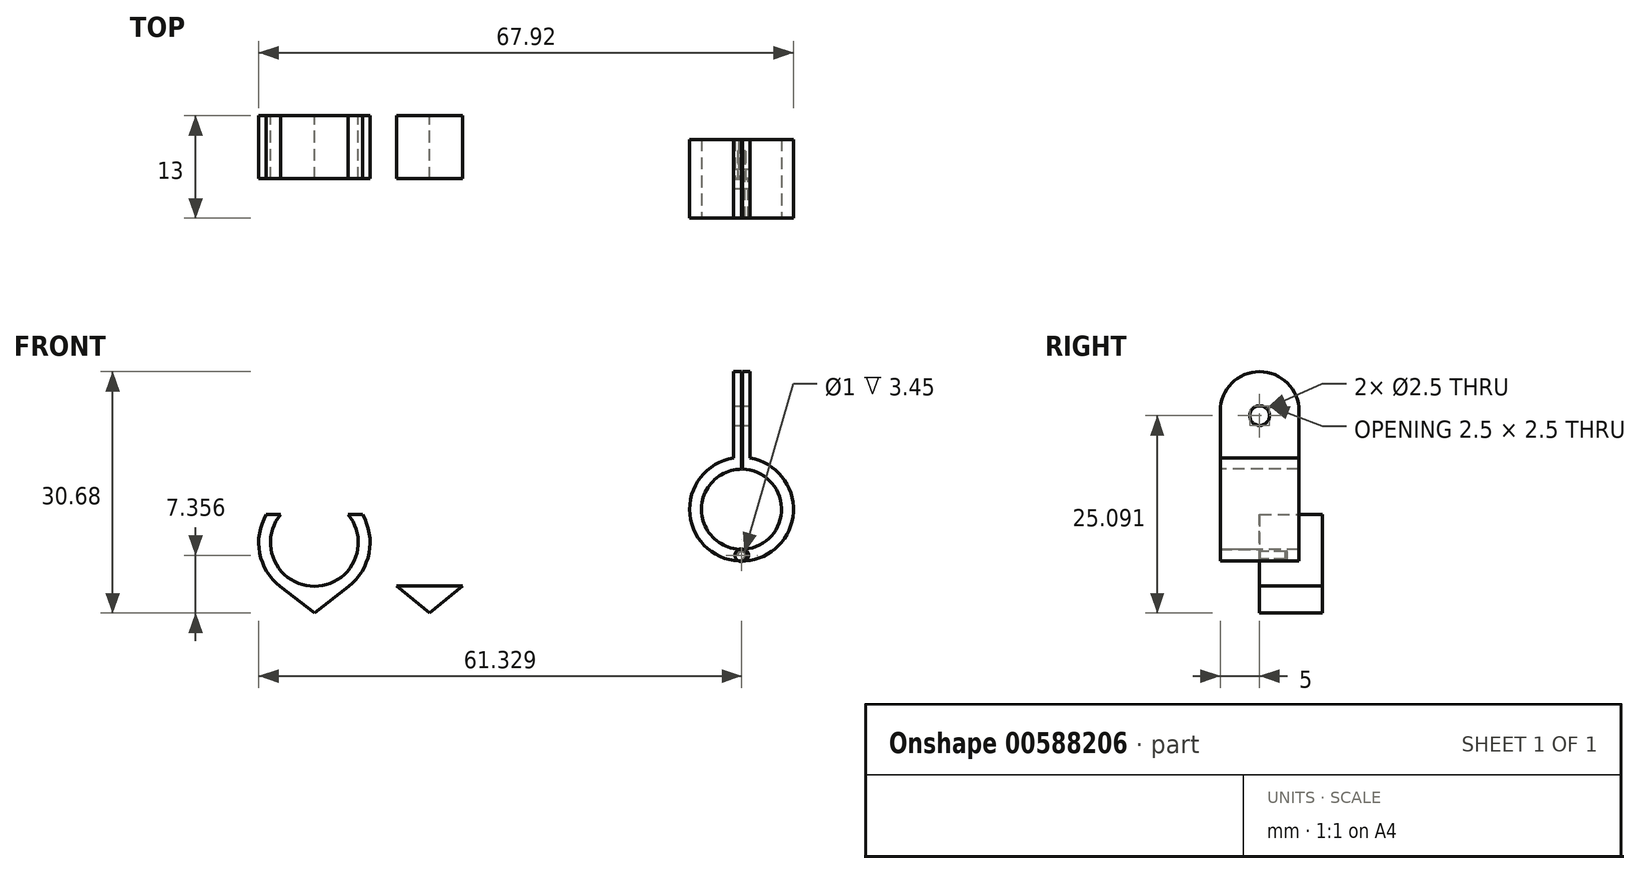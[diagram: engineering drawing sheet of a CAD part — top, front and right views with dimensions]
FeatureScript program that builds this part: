
annotation { "Feature Type Name" : "Feature", "Feature Type Description" : "" }
export const myFeature = defineFeature(function(context is Context, id is Id, definition is map)
    precondition{}
    {
        {
            var Q0;
            Q0=qCreatedBy(makeId("Front.planeOp"),FACE);
            var sketch = newSketch(context, id + "F0", { "sketchPlane" : qUnion([Q0])});
            skArc(sketch, "E0", {"start": v(-6.1, 12.53) * mm, "mid": v(0, 1.9) * mm, "end": v(6.1, 12.53) * mm});
            skLineSegment(sketch, "E1", {"start": v(-4.35, 3.4) * mm, "end": v(0, 0) * mm});
            skLineSegment(sketch, "E2", {"start": v(0, 0) * mm, "end": v(4.35, 3.4) * mm});
            skLineSegment(sketch, "E3", {"start": v(6.1, 12.53) * mm, "end": v(-6.1, 12.53) * mm});
            skArc(sketch, "E4.0", {"start": v(-4.29, 12.53) * mm, "mid": v(0, 3.4) * mm, "end": v(4.29, 12.53) * mm});
            skLineSegment(sketch, "E5", {"start": v(-5, 0) * mm, "end": v(5, 0) * mm});
            skArc(sketch, "E6", {"start": v(8.79, 11.53) * mm, "mid": v(14.66, 1.94) * mm, "end": v(20.53, 11.53) * mm});
            skLineSegment(sketch, "E7", {"start": v(10.47, 3.44) * mm, "end": v(14.66, 0) * mm});
            skLineSegment(sketch, "E8", {"start": v(14.66, 0) * mm, "end": v(18.84, 3.44) * mm});
            skLineSegment(sketch, "E9", {"start": v(20.53, 11.53) * mm, "end": v(8.79, 11.53) * mm});
            skArc(sketch, "E10.0", {"start": v(10.54, 11.53) * mm, "mid": v(14.66, 3.44) * mm, "end": v(18.78, 11.53) * mm});
            skLineSegment(sketch, "E11", {"start": v(9.66, 0) * mm, "end": v(19.66, 0) * mm});
            skLineSegment(sketch, "E12", {"start": v(14.66, 8.53) * mm, "end": v(14.66, 0) * mm});
            skLineSegment(sketch, "E13", {"start": v(-4.35, 3.4) * mm, "end": v(4.35, 3.4) * mm});
            skLineSegment(sketch, "E14", {"start": v(0, 8.97) * mm, "end": v(0, 0) * mm});
            skLineSegment(sketch, "E15", {"start": v(10.47, 3.44) * mm, "end": v(18.84, 3.44) * mm});
            skArc(sketch, "E16", {"start": v(34.1, 19.13) * mm, "mid": v(34.04, 8) * mm, "end": v(34.2, 19.13) * mm});
            skArc(sketch, "E17", {"start": v(33.1, 20.56) * mm, "mid": v(34.04, 6.5) * mm, "end": v(35.2, 20.55) * mm});
            skLineSegment(sketch, "E18", {"start": v(33.1, 19.04) * mm, "end": v(33.1, 31.04) * mm});
            skLineSegment(sketch, "E19", {"start": v(33.1, 31.04) * mm, "end": v(34.1, 31.04) * mm});
            skLineSegment(sketch, "E20", {"start": v(34.1, 31.04) * mm, "end": v(34.1, 19.13) * mm});
            skLineSegment(sketch, "E21", {"start": v(35.2, 19.02) * mm, "end": v(35.2, 31.04) * mm});
            skLineSegment(sketch, "E22", {"start": v(35.2, 31.04) * mm, "end": v(34.2, 31.04) * mm});
            skLineSegment(sketch, "E23", {"start": v(34.2, 31.04) * mm, "end": v(34.2, 19.13) * mm});
            skArc(sketch, "E24", {"start": v(53.26, 19.7) * mm, "mid": v(54.2, 6.6) * mm, "end": v(55.36, 19.7) * mm});
            skLineSegment(sketch, "E25", {"start": v(53.26, 18.19) * mm, "end": v(53.26, 30.68) * mm});
            skLineSegment(sketch, "E26", {"start": v(53.26, 30.68) * mm, "end": v(54.26, 30.68) * mm});
            skLineSegment(sketch, "E27", {"start": v(54.26, 30.68) * mm, "end": v(54.26, 18.29) * mm});
            skLineSegment(sketch, "E28", {"start": v(55.36, 18.17) * mm, "end": v(55.36, 30.68) * mm});
            skLineSegment(sketch, "E29", {"start": v(55.36, 30.68) * mm, "end": v(54.36, 30.68) * mm});
            skLineSegment(sketch, "E30", {"start": v(54.36, 30.68) * mm, "end": v(54.36, 18.28) * mm});
            skArc(sketch, "E31", {"start": v(54.26, 18.29) * mm, "mid": v(54.2, 8.1) * mm, "end": v(54.36, 18.28) * mm});
            skCircle(sketch, "E32", {"center": v(34.1, 7.24) * mm, "radius": 0.5 * mm});
            skCircle(sketch, "E33", {"center": v(54.26, 7.36) * mm, "radius": 0.5 * mm});
            skCircle(sketch, "E34", {"center": v(34.1, 7.24) * mm, "radius": 0.45 * mm});
            skCircle(sketch, "E35", {"center": v(54.26, 7.36) * mm, "radius": 0.45 * mm});
            skLineSegment(sketch, "E36", {"start": v(34.1, 8) * mm, "end": v(34.1, 6.5) * mm});
            skLineSegment(sketch, "E37", {"start": v(54.26, 8.1) * mm, "end": v(54.26, 7.86) * mm});
            skLineSegment(sketch, "E38.trimOffspring", {"start": v(54.26, 6.86) * mm, "end": v(54.26, 6.6) * mm});
            skArc(sketch, "E39", {"start": v(54, 8.11) * mm, "mid": v(53.42, 7.38) * mm, "end": v(53.97, 6.61) * mm});
            skArc(sketch, "E40", {"start": v(54.58, 6.61) * mm, "mid": v(55.09, 7.36) * mm, "end": v(54.59, 8.12) * mm});
            skArc(sketch, "E41", {"start": v(53.92, 8.12) * mm, "mid": v(53.36, 7.39) * mm, "end": v(53.86, 6.62) * mm});
            skArc(sketch, "E42", {"start": v(54.7, 6.62) * mm, "mid": v(55.15, 7.38) * mm, "end": v(54.68, 8.12) * mm});
            skSolve(sketch);
        }
        {
            var Q0;
            Q0=sQuery(id+"F0.wireOp",EDGE,"E5");
            var Q1;
            {var subQ0=sQuery(id+"F0.wireOp",EDGE,"E1");Q1=makeQuery(id+"F0.imprint","IMPRINT",FACE,{"disambiguationData":[TD([[makeQuery(id+"F0.imprint","IMPRINT",EDGE,{"derivedFrom":subQ0}),1.0]])]});}
            cPlane(context, id + "F1", {"entities" : qUnion([Q0, Q1]), "cplaneType" : CPlaneType.LINE_ANGLE, "offset" : 25 * mm, "angle" : 90 * degree, "width" : 150 * mm, "height" : 150 * mm});
        }
        {
            var Q0;
            Q0=qCreatedBy(id+"F1.planeOp",FACE);
            var sketch = newSketch(context, id + "F2", { "sketchPlane" : qUnion([Q0])});
            skLineSegment(sketch, "E43", {"start": v(0, 0) * mm, "end": v(0, 8) * mm});
            skLineSegment(sketch, "E44.0", {"start": v(9.66, 0) * mm, "end": v(19.66, 0) * mm});
            skLineSegment(sketch, "E45", {"start": v(14.66, 0) * mm, "end": v(14.66, 8) * mm});
            skSolve(sketch);
        }
        {
            var Q0;
            {var subQ0=sQuery(id+"F0.wireOp",EDGE,"E3");var subQ1=sQuery(id+"F0.wireOp",EDGE,"E0");var subQ2=makeQuery(id+"F0.imprint","INTERSECT",VERTEX,{"disambiguationData":[OD(0.0)],"derivedFrom":[subQ1,subQ0]});Q0=makeQuery(id+"F0.imprint","IMPRINT",FACE,{"disambiguationData":[TD([[makeQuery(id+"F0.imprint","IMPRINT",EDGE,{"disambiguationData":[TD([[subQ2,1.0]])],"derivedFrom":subQ0}),1.0]])]});}
            var Q1;
            {var subQ1=sQuery(id+"F0.wireOp",EDGE,"E0");var subQ3=sQuery(id+"F0.wireOp",EDGE,"E14");var subQ4=makeQuery(id+"F0.imprint","INTERSECT",VERTEX,{"derivedFrom":[subQ1,subQ3]});Q1=makeQuery(id+"F0.imprint","IMPRINT",FACE,{"disambiguationData":[TD([[makeQuery(id+"F0.imprint","IMPRINT",EDGE,{"disambiguationData":[TD([[subQ4,1.0]])],"derivedFrom":subQ1}),1.0]])]});}
            var Q2;
            {var subQ0=sQuery(id+"F0.wireOp",EDGE,"E1");Q2=makeQuery(id+"F0.imprint","IMPRINT",FACE,{"disambiguationData":[TD([[makeQuery(id+"F0.imprint","IMPRINT",EDGE,{"derivedFrom":subQ0}),1.0]])]});}
            var Q3;
            {var subQ0=sQuery(id+"F0.wireOp",EDGE,"E2");Q3=makeQuery(id+"F0.imprint","IMPRINT",FACE,{"disambiguationData":[TD([[makeQuery(id+"F0.imprint","IMPRINT",EDGE,{"derivedFrom":subQ0}),1.0]])]});}
            var Q4;
            {var subQ1=sQuery(id+"F0.wireOp",EDGE,"E0");var subQ3=sQuery(id+"F0.wireOp",EDGE,"E14");var subQ4=makeQuery(id+"F0.imprint","INTERSECT",VERTEX,{"derivedFrom":[subQ1,subQ3]});Q4=makeQuery(id+"F0.imprint","IMPRINT",FACE,{"disambiguationData":[TD([[makeQuery(id+"F0.imprint","IMPRINT",EDGE,{"disambiguationData":[TD([[subQ4,-1.0]])],"derivedFrom":subQ1}),1.0]])]});}
            var Q5;
            {var subQ0=sQuery(id+"F0.wireOp",EDGE,"E3");var subQ1=sQuery(id+"F0.wireOp",EDGE,"E0");var subQ2=makeQuery(id+"F0.imprint","INTERSECT",VERTEX,{"disambiguationData":[OD(1.0)],"derivedFrom":[subQ1,subQ0]});Q5=makeQuery(id+"F0.imprint","IMPRINT",FACE,{"disambiguationData":[TD([[makeQuery(id+"F0.imprint","IMPRINT",EDGE,{"disambiguationData":[TD([[subQ2,-1.0]])],"derivedFrom":subQ0}),1.0]])]});}
            var Q6;
            Q6=sQuery(id+"F2.wireOp",EDGE,"E43");
            sweep(context, id + "F3", {"profiles" : qUnion([Q0, Q1, Q2, Q3, Q4, Q5]), "path" : qUnion([Q6])});
        }
        {
            var Q0;
            {var subQ0=sQuery(id+"F0.wireOp",EDGE,"E9");var subQ1=sQuery(id+"F0.wireOp",EDGE,"E6");var subQ2=makeQuery(id+"F0.imprint","INTERSECT",VERTEX,{"disambiguationData":[OD(0.0)],"derivedFrom":[subQ1,subQ0]});Q0=makeQuery(id+"F0.imprint","IMPRINT",FACE,{"disambiguationData":[TD([[makeQuery(id+"F0.imprint","IMPRINT",EDGE,{"disambiguationData":[TD([[subQ2,1.0]])],"derivedFrom":subQ0}),1.0]])]});}
            var Q1;
            {var subQ1=sQuery(id+"F0.wireOp",EDGE,"E6");var subQ3=sQuery(id+"F0.wireOp",EDGE,"E12");var subQ4=makeQuery(id+"F0.imprint","INTERSECT",VERTEX,{"derivedFrom":[subQ1,subQ3]});Q1=makeQuery(id+"F0.imprint","IMPRINT",FACE,{"disambiguationData":[TD([[makeQuery(id+"F0.imprint","IMPRINT",EDGE,{"disambiguationData":[TD([[subQ4,1.0]])],"derivedFrom":subQ1}),1.0]])]});}
            var Q2;
            {var subQ0=sQuery(id+"F0.wireOp",EDGE,"E7");Q2=makeQuery(id+"F0.imprint","IMPRINT",FACE,{"disambiguationData":[TD([[makeQuery(id+"F0.imprint","IMPRINT",EDGE,{"derivedFrom":subQ0}),1.0]])]});}
            var Q3;
            {var subQ0=sQuery(id+"F0.wireOp",EDGE,"E8");Q3=makeQuery(id+"F0.imprint","IMPRINT",FACE,{"disambiguationData":[TD([[makeQuery(id+"F0.imprint","IMPRINT",EDGE,{"derivedFrom":subQ0}),1.0]])]});}
            var Q4;
            {var subQ1=sQuery(id+"F0.wireOp",EDGE,"E6");var subQ3=sQuery(id+"F0.wireOp",EDGE,"E12");var subQ4=makeQuery(id+"F0.imprint","INTERSECT",VERTEX,{"derivedFrom":[subQ1,subQ3]});Q4=makeQuery(id+"F0.imprint","IMPRINT",FACE,{"disambiguationData":[TD([[makeQuery(id+"F0.imprint","IMPRINT",EDGE,{"disambiguationData":[TD([[subQ4,-1.0]])],"derivedFrom":subQ1}),1.0]])]});}
            var Q5;
            {var subQ0=sQuery(id+"F0.wireOp",EDGE,"E9");var subQ1=sQuery(id+"F0.wireOp",EDGE,"E6");var subQ2=makeQuery(id+"F0.imprint","INTERSECT",VERTEX,{"disambiguationData":[OD(1.0)],"derivedFrom":[subQ1,subQ0]});Q5=makeQuery(id+"F0.imprint","IMPRINT",FACE,{"disambiguationData":[TD([[makeQuery(id+"F0.imprint","IMPRINT",EDGE,{"disambiguationData":[TD([[subQ2,-1.0]])],"derivedFrom":subQ0}),1.0]])]});}
            var Q6;
            Q6=sQuery(id+"F2.wireOp",EDGE,"E45");
            sweep(context, id + "F4", {"profiles" : qUnion([Q0, Q1, Q2, Q3, Q4, Q5]), "path" : qUnion([Q6])});
        }
        {
            var Q0;
            {var subQ0=sQuery(id+"F0.wireOp",EDGE,"E25");var subQ1=sQuery(id+"F0.wireOp",EDGE,"E24");var subQ2=makeQuery(id+"F0.imprint","INTERSECT",VERTEX,{"derivedFrom":[subQ1,subQ0]});Q0=makeQuery(id+"F0.imprint","IMPRINT",FACE,{"disambiguationData":[TD([[makeQuery(id+"F0.imprint","IMPRINT",EDGE,{"disambiguationData":[TD([[subQ2,-1.0]])],"derivedFrom":subQ1}),1.0]])]});}
            var Q1;
            {var subQ1=sQuery(id+"F0.wireOp",EDGE,"E26");Q1=makeQuery(id+"F0.imprint","IMPRINT",FACE,{"disambiguationData":[TD([[makeQuery(id+"F0.imprint","IMPRINT",EDGE,{"derivedFrom":subQ1}),-1.0]])]});}
            var Q2;
            {var subQ1=sQuery(id+"F0.wireOp",EDGE,"E29");Q2=makeQuery(id+"F0.imprint","IMPRINT",FACE,{"disambiguationData":[TD([[makeQuery(id+"F0.imprint","IMPRINT",EDGE,{"derivedFrom":subQ1}),1.0]])]});}
            var Q3;
            {var subQ0=sQuery(id+"F0.wireOp",EDGE,"7ITHiso8-4JlL-8OCp-N88B-hGmzVnLDeb8b");var subQ1=sQuery(id+"F0.wireOp",EDGE,"E24");var subQ2=makeQuery(id+"F0.imprint","INTERSECT",VERTEX,{"derivedFrom":[subQ1,subQ0]});Q3=makeQuery(id+"F0.imprint","IMPRINT",FACE,{"disambiguationData":[TD([[makeQuery(id+"F0.imprint","IMPRINT",EDGE,{"disambiguationData":[TD([[subQ2,1.0]])],"derivedFrom":subQ1}),1.0]])]});}
            var Q4;
            {var subQ0=sQuery(id+"F0.wireOp",EDGE,"7ITHiso8-4JlL-8OCp-N88B-hGmzVnLDeb8b");var subQ1=sQuery(id+"F0.wireOp",EDGE,"E33");var subQ2=makeQuery(id+"F0.imprint","INTERSECT",VERTEX,{"disambiguationData":[OD(0.0)],"derivedFrom":[subQ1,subQ0]});Q4=makeQuery(id+"F0.imprint","IMPRINT",FACE,{"disambiguationData":[TD([[makeQuery(id+"F0.imprint","IMPRINT",EDGE,{"disambiguationData":[TD([[subQ2,1.0]])],"derivedFrom":subQ1}),1.0]])]});}
            var Q5;
            {var subQ0=sQuery(id+"F0.wireOp",EDGE,"7ITHiso8-4JlL-8OCp-N88B-hGmzVnLDeb8b");var subQ1=sQuery(id+"F0.wireOp",EDGE,"E35");var subQ2=makeQuery(id+"F0.imprint","INTERSECT",VERTEX,{"disambiguationData":[OD(0.0)],"derivedFrom":[subQ1,subQ0]});Q5=makeQuery(id+"F0.imprint","IMPRINT",FACE,{"disambiguationData":[TD([[makeQuery(id+"F0.imprint","IMPRINT",EDGE,{"disambiguationData":[TD([[subQ2,1.0]])],"derivedFrom":subQ1}),1.0]])]});}
            var Q6;
            {var subQ0=sQuery(id+"F0.wireOp",EDGE,"cSInmPlT-iqMw-8Al4-92XP-XwhJxrcbgfqi");var subQ1=sQuery(id+"F0.wireOp",EDGE,"E35");var subQ2=makeQuery(id+"F0.imprint","INTERSECT",VERTEX,{"disambiguationData":[OD(0.0)],"derivedFrom":[subQ1,subQ0]});Q6=makeQuery(id+"F0.imprint","IMPRINT",FACE,{"disambiguationData":[TD([[makeQuery(id+"F0.imprint","IMPRINT",EDGE,{"disambiguationData":[TD([[subQ2,1.0]])],"derivedFrom":subQ1}),1.0]])]});}
            var Q7;
            {var subQ0=sQuery(id+"F0.wireOp",EDGE,"cSInmPlT-iqMw-8Al4-92XP-XwhJxrcbgfqi");var subQ1=sQuery(id+"F0.wireOp",EDGE,"E35");var subQ2=makeQuery(id+"F0.imprint","INTERSECT",VERTEX,{"disambiguationData":[OD(0.0)],"derivedFrom":[subQ1,subQ0]});Q7=makeQuery(id+"F0.imprint","IMPRINT",FACE,{"disambiguationData":[TD([[makeQuery(id+"F0.imprint","IMPRINT",EDGE,{"disambiguationData":[TD([[subQ2,-1.0]])],"derivedFrom":subQ1}),1.0]])]});}
            var Q8;
            {var subQ0=sQuery(id+"F0.wireOp",EDGE,"cSInmPlT-iqMw-8Al4-92XP-XwhJxrcbgfqi");var subQ1=sQuery(id+"F0.wireOp",EDGE,"E33");var subQ2=makeQuery(id+"F0.imprint","INTERSECT",VERTEX,{"disambiguationData":[OD(0.0)],"derivedFrom":[subQ1,subQ0]});Q8=makeQuery(id+"F0.imprint","IMPRINT",FACE,{"disambiguationData":[TD([[makeQuery(id+"F0.imprint","IMPRINT",EDGE,{"disambiguationData":[TD([[subQ2,1.0]])],"derivedFrom":subQ1}),1.0]])]});}
            var Q9;
            {var subQ0=sQuery(id+"F0.wireOp",EDGE,"cSInmPlT-iqMw-8Al4-92XP-XwhJxrcbgfqi");var subQ1=sQuery(id+"F0.wireOp",EDGE,"E33");var subQ2=makeQuery(id+"F0.imprint","INTERSECT",VERTEX,{"disambiguationData":[OD(1.0)],"derivedFrom":[subQ1,subQ0]});Q9=makeQuery(id+"F0.imprint","IMPRINT",FACE,{"disambiguationData":[TD([[makeQuery(id+"F0.imprint","IMPRINT",EDGE,{"disambiguationData":[TD([[subQ2,-1.0]])],"derivedFrom":subQ1}),1.0]])]});}
            var Q10;
            {var subQ0=sQuery(id+"F0.wireOp",EDGE,"cSInmPlT-iqMw-8Al4-92XP-XwhJxrcbgfqi");var subQ1=sQuery(id+"F0.wireOp",EDGE,"E33");var subQ2=makeQuery(id+"F0.imprint","INTERSECT",VERTEX,{"disambiguationData":[OD(0.0)],"derivedFrom":[subQ1,subQ0]});Q10=makeQuery(id+"F0.imprint","IMPRINT",FACE,{"disambiguationData":[TD([[makeQuery(id+"F0.imprint","IMPRINT",EDGE,{"disambiguationData":[TD([[subQ2,-1.0]])],"derivedFrom":subQ1}),1.0]])]});}
            var Q11;
            {var subQ5=sQuery(id+"F0.wireOp",EDGE,"E28");var subQ8=sQuery(id+"F0.wireOp",EDGE,"E24");var subQ9=makeQuery(id+"F0.imprint","INTERSECT",VERTEX,{"derivedFrom":[subQ8,subQ5]});Q11=makeQuery(id+"F0.imprint","IMPRINT",FACE,{"disambiguationData":[TD([[makeQuery(id+"F0.imprint","IMPRINT",EDGE,{"disambiguationData":[TD([[subQ9,1.0]])],"derivedFrom":subQ8}),1.0]])]});}
            var Q12;
            {var subQ0=sQuery(id+"F0.wireOp",EDGE,"7ITHiso8-4JlL-8OCp-N88B-hGmzVnLDeb8b");var subQ1=sQuery(id+"F0.wireOp",EDGE,"E31");var subQ2=makeQuery(id+"F0.imprint","INTERSECT",VERTEX,{"derivedFrom":[subQ1,subQ0]});Q12=makeQuery(id+"F0.imprint","IMPRINT",FACE,{"disambiguationData":[TD([[makeQuery(id+"F0.imprint","IMPRINT",EDGE,{"disambiguationData":[TD([[subQ2,1.0]])],"derivedFrom":subQ1}),-1.0]])]});}
            var Q13;
            {var subQ0=sQuery(id+"F0.wireOp",EDGE,"E37");Q13=makeQuery(id+"F0.imprint","IMPRINT",FACE,{"disambiguationData":[TD([[makeQuery(id+"F0.imprint","IMPRINT",EDGE,{"derivedFrom":subQ0}),-1.0]])]});}
            var Q14;
            {var subQ0=sQuery(id+"F0.wireOp",EDGE,"E37");Q14=makeQuery(id+"F0.imprint","IMPRINT",FACE,{"disambiguationData":[TD([[makeQuery(id+"F0.imprint","IMPRINT",EDGE,{"derivedFrom":subQ0}),1.0]])]});}
            var Q15;
            Q15=makeQuery(id+"F0.imprint","IMPRINT",FACE,{"disambiguationData":[TD([[makeQuery(id+"F0.imprint","IMPRINT",EDGE,{"derivedFrom":sQuery(id+"F0.wireOp",EDGE,"E35")}),1.0]])]});
            extrude(context, id + "F5", {"entities" : qUnion([Q0, Q1, Q2, Q3, Q4, Q5, Q6, Q7, Q8, Q9, Q10, Q11, Q12, Q13, Q14, Q15]), "oppositeDirection" : true, "depth" : 5 * mm, "offsetDistance" : 25 * mm});
        }
        {
            var Q0;
            Q0=makeQuery(id+"F0.imprint","IMPRINT",FACE,{"disambiguationData":[TD([[makeQuery(id+"F0.imprint","IMPRINT",EDGE,{"derivedFrom":sQuery(id+"F0.wireOp",EDGE,"E35")}),-1.0]])]});
            var Q1;
            Q1=makeQuery(id+"F0.imprint","IMPRINT",FACE,{"disambiguationData":[TD([[makeQuery(id+"F0.imprint","IMPRINT",EDGE,{"derivedFrom":sQuery(id+"F0.wireOp",EDGE,"E35")}),1.0]])]});
            extrude(context, id + "F6", {"entities" : qUnion([Q0, Q1]), "operationType" : NewBodyOperationType.REMOVE, "oppositeDirection" : true, "depth" : 3.5 * mm, "offsetDistance" : 25 * mm});
        }
        {
            var Q0;
            {var subQ5=sQuery(id+"F0.wireOp",EDGE,"E28");var subQ8=sQuery(id+"F0.wireOp",EDGE,"E24");var subQ9=makeQuery(id+"F0.imprint","INTERSECT",VERTEX,{"derivedFrom":[subQ8,subQ5]});Q0=makeQuery(id+"F0.imprint","IMPRINT",FACE,{"disambiguationData":[TD([[makeQuery(id+"F0.imprint","IMPRINT",EDGE,{"disambiguationData":[TD([[subQ9,1.0]])],"derivedFrom":subQ8}),1.0]])]});}
            var Q1;
            {var subQ5=sQuery(id+"F0.wireOp",EDGE,"E25");var subQ8=sQuery(id+"F0.wireOp",EDGE,"E24");var subQ9=makeQuery(id+"F0.imprint","INTERSECT",VERTEX,{"derivedFrom":[subQ8,subQ5]});Q1=makeQuery(id+"F0.imprint","IMPRINT",FACE,{"disambiguationData":[TD([[makeQuery(id+"F0.imprint","IMPRINT",EDGE,{"disambiguationData":[TD([[subQ9,-1.0]])],"derivedFrom":subQ8}),1.0]])]});}
            var Q2;
            {var subQ1=sQuery(id+"F0.wireOp",EDGE,"E26");Q2=makeQuery(id+"F0.imprint","IMPRINT",FACE,{"disambiguationData":[TD([[makeQuery(id+"F0.imprint","IMPRINT",EDGE,{"derivedFrom":subQ1}),-1.0]])]});}
            var Q3;
            {var subQ1=sQuery(id+"F0.wireOp",EDGE,"E29");Q3=makeQuery(id+"F0.imprint","IMPRINT",FACE,{"disambiguationData":[TD([[makeQuery(id+"F0.imprint","IMPRINT",EDGE,{"derivedFrom":subQ1}),1.0]])]});}
            var Q4;
            {var subQ0=sQuery(id+"F0.wireOp",EDGE,"7ITHiso8-4JlL-8OCp-N88B-hGmzVnLDeb8b");var subQ1=sQuery(id+"F0.wireOp",EDGE,"E24");var subQ2=makeQuery(id+"F0.imprint","INTERSECT",VERTEX,{"derivedFrom":[subQ1,subQ0]});Q4=makeQuery(id+"F0.imprint","IMPRINT",FACE,{"disambiguationData":[TD([[makeQuery(id+"F0.imprint","IMPRINT",EDGE,{"disambiguationData":[TD([[subQ2,1.0]])],"derivedFrom":subQ1}),1.0]])]});}
            var Q5;
            {var subQ0=sQuery(id+"F0.wireOp",EDGE,"7ITHiso8-4JlL-8OCp-N88B-hGmzVnLDeb8b");var subQ1=sQuery(id+"F0.wireOp",EDGE,"E35");var subQ2=makeQuery(id+"F0.imprint","INTERSECT",VERTEX,{"disambiguationData":[OD(0.0)],"derivedFrom":[subQ1,subQ0]});Q5=makeQuery(id+"F0.imprint","IMPRINT",FACE,{"disambiguationData":[TD([[makeQuery(id+"F0.imprint","IMPRINT",EDGE,{"disambiguationData":[TD([[subQ2,1.0]])],"derivedFrom":subQ1}),1.0]])]});}
            var Q6;
            {var subQ0=sQuery(id+"F0.wireOp",EDGE,"cSInmPlT-iqMw-8Al4-92XP-XwhJxrcbgfqi");var subQ1=sQuery(id+"F0.wireOp",EDGE,"E35");var subQ2=makeQuery(id+"F0.imprint","INTERSECT",VERTEX,{"disambiguationData":[OD(0.0)],"derivedFrom":[subQ1,subQ0]});Q6=makeQuery(id+"F0.imprint","IMPRINT",FACE,{"disambiguationData":[TD([[makeQuery(id+"F0.imprint","IMPRINT",EDGE,{"disambiguationData":[TD([[subQ2,1.0]])],"derivedFrom":subQ1}),1.0]])]});}
            var Q7;
            {var subQ0=sQuery(id+"F0.wireOp",EDGE,"cSInmPlT-iqMw-8Al4-92XP-XwhJxrcbgfqi");var subQ1=sQuery(id+"F0.wireOp",EDGE,"E35");var subQ2=makeQuery(id+"F0.imprint","INTERSECT",VERTEX,{"disambiguationData":[OD(0.0)],"derivedFrom":[subQ1,subQ0]});Q7=makeQuery(id+"F0.imprint","IMPRINT",FACE,{"disambiguationData":[TD([[makeQuery(id+"F0.imprint","IMPRINT",EDGE,{"disambiguationData":[TD([[subQ2,-1.0]])],"derivedFrom":subQ1}),1.0]])]});}
            var Q8;
            {var subQ0=sQuery(id+"F0.wireOp",EDGE,"7ITHiso8-4JlL-8OCp-N88B-hGmzVnLDeb8b");var subQ1=sQuery(id+"F0.wireOp",EDGE,"E33");var subQ2=makeQuery(id+"F0.imprint","INTERSECT",VERTEX,{"disambiguationData":[OD(0.0)],"derivedFrom":[subQ1,subQ0]});Q8=makeQuery(id+"F0.imprint","IMPRINT",FACE,{"disambiguationData":[TD([[makeQuery(id+"F0.imprint","IMPRINT",EDGE,{"disambiguationData":[TD([[subQ2,1.0]])],"derivedFrom":subQ1}),1.0]])]});}
            var Q9;
            {var subQ0=sQuery(id+"F0.wireOp",EDGE,"cSInmPlT-iqMw-8Al4-92XP-XwhJxrcbgfqi");var subQ1=sQuery(id+"F0.wireOp",EDGE,"E33");var subQ2=makeQuery(id+"F0.imprint","INTERSECT",VERTEX,{"disambiguationData":[OD(0.0)],"derivedFrom":[subQ1,subQ0]});Q9=makeQuery(id+"F0.imprint","IMPRINT",FACE,{"disambiguationData":[TD([[makeQuery(id+"F0.imprint","IMPRINT",EDGE,{"disambiguationData":[TD([[subQ2,1.0]])],"derivedFrom":subQ1}),1.0]])]});}
            var Q10;
            {var subQ0=sQuery(id+"F0.wireOp",EDGE,"7ITHiso8-4JlL-8OCp-N88B-hGmzVnLDeb8b");var subQ1=sQuery(id+"F0.wireOp",EDGE,"E31");var subQ2=makeQuery(id+"F0.imprint","INTERSECT",VERTEX,{"derivedFrom":[subQ1,subQ0]});Q10=makeQuery(id+"F0.imprint","IMPRINT",FACE,{"disambiguationData":[TD([[makeQuery(id+"F0.imprint","IMPRINT",EDGE,{"disambiguationData":[TD([[subQ2,1.0]])],"derivedFrom":subQ1}),-1.0]])]});}
            var Q11;
            {var subQ0=sQuery(id+"F0.wireOp",EDGE,"cSInmPlT-iqMw-8Al4-92XP-XwhJxrcbgfqi");var subQ1=sQuery(id+"F0.wireOp",EDGE,"E33");var subQ2=makeQuery(id+"F0.imprint","INTERSECT",VERTEX,{"disambiguationData":[OD(0.0)],"derivedFrom":[subQ1,subQ0]});Q11=makeQuery(id+"F0.imprint","IMPRINT",FACE,{"disambiguationData":[TD([[makeQuery(id+"F0.imprint","IMPRINT",EDGE,{"disambiguationData":[TD([[subQ2,-1.0]])],"derivedFrom":subQ1}),1.0]])]});}
            var Q12;
            {var subQ0=sQuery(id+"F0.wireOp",EDGE,"cSInmPlT-iqMw-8Al4-92XP-XwhJxrcbgfqi");var subQ1=sQuery(id+"F0.wireOp",EDGE,"E33");var subQ2=makeQuery(id+"F0.imprint","INTERSECT",VERTEX,{"disambiguationData":[OD(1.0)],"derivedFrom":[subQ1,subQ0]});Q12=makeQuery(id+"F0.imprint","IMPRINT",FACE,{"disambiguationData":[TD([[makeQuery(id+"F0.imprint","IMPRINT",EDGE,{"disambiguationData":[TD([[subQ2,-1.0]])],"derivedFrom":subQ1}),1.0]])]});}
            var Q13;
            {var subQ0=sQuery(id+"F0.wireOp",EDGE,"E37");Q13=makeQuery(id+"F0.imprint","IMPRINT",FACE,{"disambiguationData":[TD([[makeQuery(id+"F0.imprint","IMPRINT",EDGE,{"derivedFrom":subQ0}),1.0]])]});}
            var Q14;
            {var subQ0=sQuery(id+"F0.wireOp",EDGE,"E37");Q14=makeQuery(id+"F0.imprint","IMPRINT",FACE,{"disambiguationData":[TD([[makeQuery(id+"F0.imprint","IMPRINT",EDGE,{"derivedFrom":subQ0}),-1.0]])]});}
            var Q15;
            Q15=makeQuery(id+"F0.imprint","IMPRINT",FACE,{"disambiguationData":[TD([[makeQuery(id+"F0.imprint","IMPRINT",EDGE,{"derivedFrom":sQuery(id+"F0.wireOp",EDGE,"E35")}),1.0]])]});
            extrude(context, id + "F7", {"entities" : qUnion([Q0, Q1, Q2, Q3, Q4, Q5, Q6, Q7, Q8, Q9, Q10, Q11, Q12, Q13, Q14, Q15]), "operationType" : NewBodyOperationType.ADD, "depth" : 5 * mm, "offsetDistance" : 25 * mm});
        }
        {
            var Q0;
            Q0=makeQuery(id+"F0.imprint","IMPRINT",FACE,{"disambiguationData":[TD([[makeQuery(id+"F0.imprint","IMPRINT",EDGE,{"derivedFrom":sQuery(id+"F0.wireOp",EDGE,"E35")}),1.0]])]});
            extrude(context, id + "F8", {"entities" : qUnion([Q0]), "operationType" : NewBodyOperationType.ADD, "oppositeDirection" : true, "depth" : 3.3 * mm, "offsetDistance" : 25 * mm});
        }
        {
            var Q0;
            {var subQ0=sQuery(id+"F0.wireOp",EDGE,"E40");Q0=makeQuery(id+"F0.imprint","IMPRINT",FACE,{"disambiguationData":[TD([[makeQuery(id+"F0.imprint","IMPRINT",EDGE,{"derivedFrom":subQ0}),-1.0]])]});}
            extrude(context, id + "F9", {"entities" : qUnion([Q0]), "operationType" : NewBodyOperationType.REMOVE, "endBound" : BoundingType.THROUGH_ALL, "depth" : 25 * mm, "offsetDistance" : 25 * mm});
        }
        {
            var Q0;
            {var subQ0=sQuery(id+"F0.wireOp",EDGE,"E39");Q0=makeQuery(id+"F0.imprint","IMPRINT",FACE,{"disambiguationData":[TD([[makeQuery(id+"F0.imprint","IMPRINT",EDGE,{"derivedFrom":subQ0}),-1.0]])]});}
            extrude(context, id + "F10", {"entities" : qUnion([Q0]), "operationType" : NewBodyOperationType.REMOVE, "endBound" : BoundingType.THROUGH_ALL, "oppositeDirection" : true, "depth" : 25 * mm, "offsetDistance" : 25 * mm});
        }
        {
            var Q0;
            {var subQ0=sQuery(id+"F0.wireOp",EDGE,"E37");Q0=makeQuery(id+"F0.imprint","IMPRINT",FACE,{"disambiguationData":[TD([[makeQuery(id+"F0.imprint","IMPRINT",EDGE,{"derivedFrom":subQ0}),1.0]])]});}
            var Q1;
            {var subQ0=sQuery(id+"F0.wireOp",EDGE,"E37");Q1=makeQuery(id+"F0.imprint","IMPRINT",FACE,{"disambiguationData":[TD([[makeQuery(id+"F0.imprint","IMPRINT",EDGE,{"derivedFrom":subQ0}),-1.0]])]});}
            extrude(context, id + "F11", {"entities" : qUnion([Q0, Q1]), "operationType" : NewBodyOperationType.REMOVE, "endBound" : BoundingType.SYMMETRIC, "oppositeDirection" : true, "depth" : 0.1 * mm, "offsetDistance" : 25 * mm});
        }
        {
            var Q0;
            {var subQ0=sQuery(id+"F0.wireOp",EDGE,"E28");Q0=makeQuery(id+"F7.boolean.opBoolean","MERGE",FACE,{"derivedFrom":[makeQuery(id+"F5.opExtrude","SWEPT_FACE",FACE,{"disambiguationData":[OSD([subQ0])]}),makeQuery(id+"F7.opExtrude","SWEPT_FACE",FACE,{"disambiguationData":[OSD([subQ0])]})]});}
            var sketch = newSketch(context, id + "F12", { "sketchPlane" : qUnion([Q0])});
            skCircle(sketch, "E46", {"center": v(0, 25.1) * mm, "radius": 1.25 * mm});
            skSolve(sketch);
        }
        {
            var Q0;
            Q0=makeQuery(id+"F12.imprint","IMPRINT",FACE,{"disambiguationData":[TD([[makeQuery(id+"F12.imprint","IMPRINT",EDGE,{"derivedFrom":sQuery(id+"F12.wireOp",EDGE,"E46")}),1.0]])]});
            extrude(context, id + "F13", {"entities" : qUnion([Q0]), "operationType" : NewBodyOperationType.REMOVE, "endBound" : BoundingType.THROUGH_ALL, "oppositeDirection" : true, "depth" : 25 * mm, "offsetDistance" : 25 * mm});
        }
        {
            var Q0;
            Q0=makeQuery(id+"F7.opExtrude","CAP_EDGE",EDGE,{"disambiguationData":[OSD([sQuery(id+"F0.wireOp",EDGE,"E26")])],"isStart":false});
            var Q1;
            Q1=makeQuery(id+"F7.opExtrude","CAP_EDGE",EDGE,{"disambiguationData":[OSD([sQuery(id+"F0.wireOp",EDGE,"E29")])],"isStart":false});
            var Q2;
            Q2=makeQuery(id+"F5.opExtrude","CAP_EDGE",EDGE,{"disambiguationData":[OSD([sQuery(id+"F0.wireOp",EDGE,"E26")])],"isStart":false});
            var Q3;
            Q3=makeQuery(id+"F5.opExtrude","CAP_EDGE",EDGE,{"disambiguationData":[OSD([sQuery(id+"F0.wireOp",EDGE,"E29")])],"isStart":false});
            fillet(context, id + "F14", {"entities" : qUnion([Q0, Q1, Q2, Q3]), "radius" : 5 * mm, "tangentPropagation" : true, "allowEdgeOverflow" : false});
        }
    });
